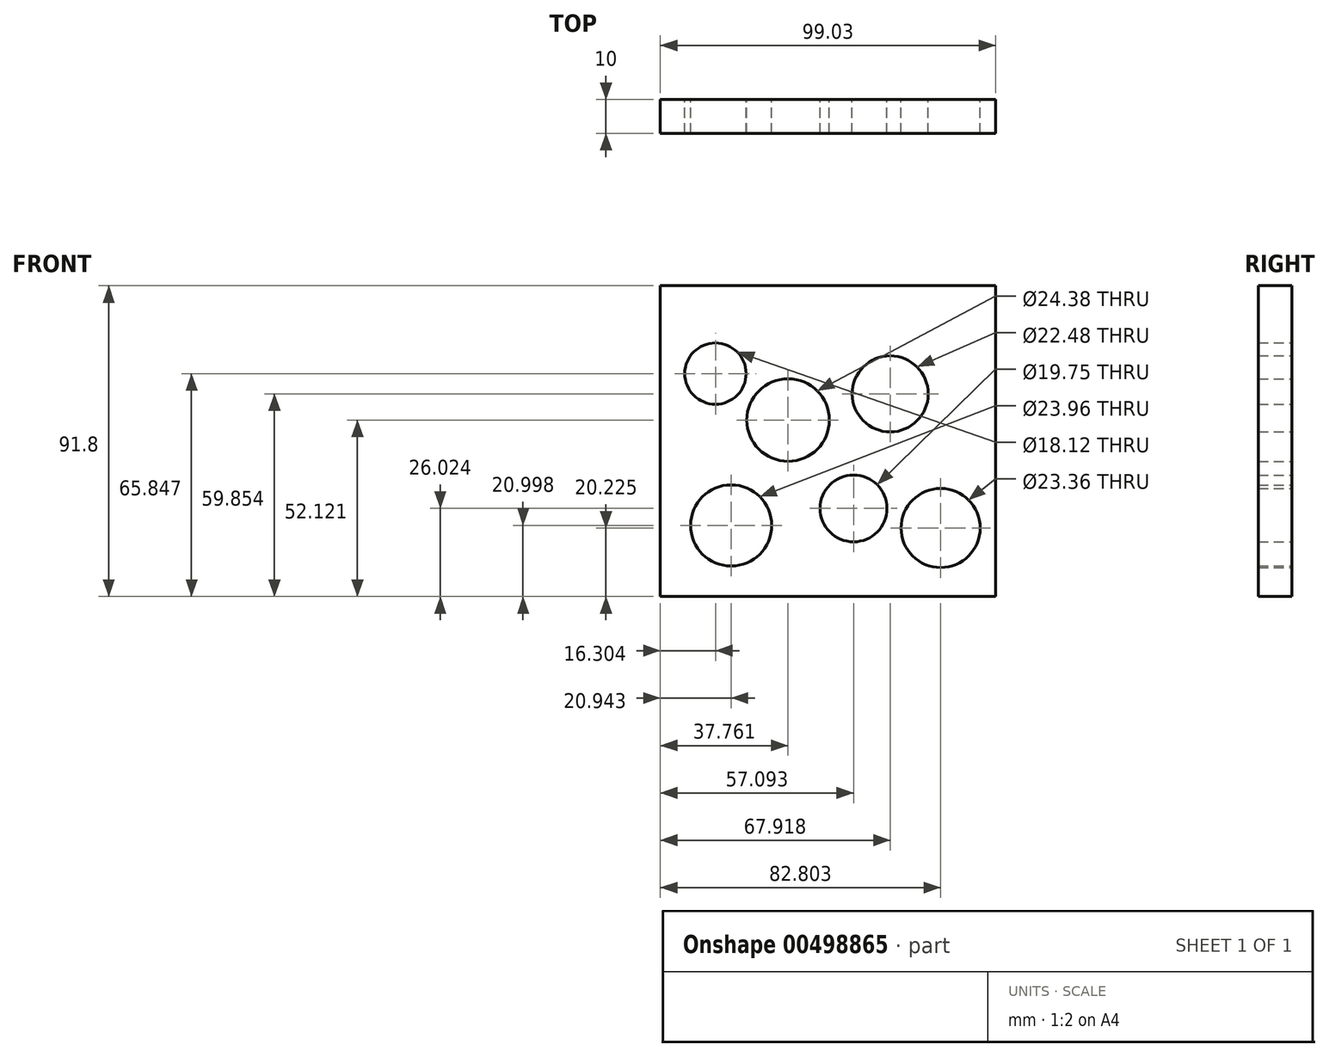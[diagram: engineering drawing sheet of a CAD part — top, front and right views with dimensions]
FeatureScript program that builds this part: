
annotation { "Feature Type Name" : "Feature", "Feature Type Description" : "" }
export const myFeature = defineFeature(function(context is Context, id is Id, definition is map)
    precondition{}
    {
        {
            var Q0;
            Q0=qCreatedBy(makeId("Front.planeOp"),FACE);
            var sketch = newSketch(context, id + "F0", { "sketchPlane" : qUnion([Q0])});
            skLineSegment(sketch, "E0.bottom", {"start": v(0, 0) * mm, "end": v(-99.03, 0) * mm});
            skLineSegment(sketch, "E0.top", {"start": v(0, 91.8) * mm, "end": v(-99.03, 91.8) * mm});
            skLineSegment(sketch, "E0.left", {"start": v(0, 0) * mm, "end": v(0, 91.8) * mm});
            skLineSegment(sketch, "E0.right", {"start": v(-99.03, 0) * mm, "end": v(-99.03, 91.8) * mm});
            skCircle(sketch, "E1", {"center": v(-61.27, 52.12) * mm, "radius": 12.2 * mm});
            skCircle(sketch, "E2", {"center": v(-31.11, 59.85) * mm, "radius": 11.24 * mm});
            skCircle(sketch, "E3", {"center": v(-41.94, 26.02) * mm, "radius": 9.87 * mm});
            skCircle(sketch, "E4", {"center": v(-78.09, 21) * mm, "radius": 11.98 * mm});
            skCircle(sketch, "E5", {"center": v(-82.73, 65.85) * mm, "radius": 9.06 * mm});
            skCircle(sketch, "E6", {"center": v(-16.23, 20.22) * mm, "radius": 11.68 * mm});
            skSolve(sketch);
        }
        {
            var Q0;
            Q0=makeQuery(id+"F0.imprint","IMPRINT",FACE,{"disambiguationData":[TD([[makeQuery(id+"F0.imprint","IMPRINT",EDGE,{"derivedFrom":sQuery(id+"F0.wireOp",EDGE,"E0.bottom")}),-1.0]])]});
            extrude(context, id + "F1", {"entities" : qUnion([Q0]), "depth" : 10 * mm, "offsetDistance" : 25 * mm});
        }
    });
